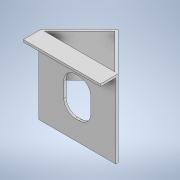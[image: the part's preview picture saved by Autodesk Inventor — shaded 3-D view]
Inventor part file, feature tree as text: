
AUTODESK INVENTOR PART (.ipt)
format: ipt  version: 2020 (Build 240168000, 168)  size: 140,288 bytes
history: native  units: mm
features: extrude x4, sketch x4
ambient origin geometry x8: Origin, YZ Plane, XZ Plane, XY Plane, X Axis, Y Axis, Z Axis, Center Point
bodies: Solid1 (feature_tree)
feature tree (8):
  extrude  "Extrusion1"  Depth=100.0mm
  extrude  "Extrusion2"  TaperAngle=45.0deg  [1 undecoded]
  extrude  "Extrusion3"  Depth=3.0mm
  extrude  "Extrusion5"  Depth=35.0mm
  sketch  "Sketch1"  dims[d0=100.0mm d1=100.0mm]
  sketch  "Sketch2"  dims[d2=3.0mm d3=0.0mm d4=45.0deg]
  sketch  "Sketch3"  dims[d5=3.0mm d6=3.0mm]
  sketch  "Sketch5"  dims[d7=55.0mm d8=0.0mm d9=35.0mm d10=50.0mm d11=15.0mm d12=3.0mm d13=0.0mm d16=100.0mm d17=20.0mm d18=3.0mm d19=0.0mm]
note: 1 required parameter value undecoded (feature->parameter linkage not recoverable at this tier; creation-order binding heuristic only, values carry confidence <= 0.55)
